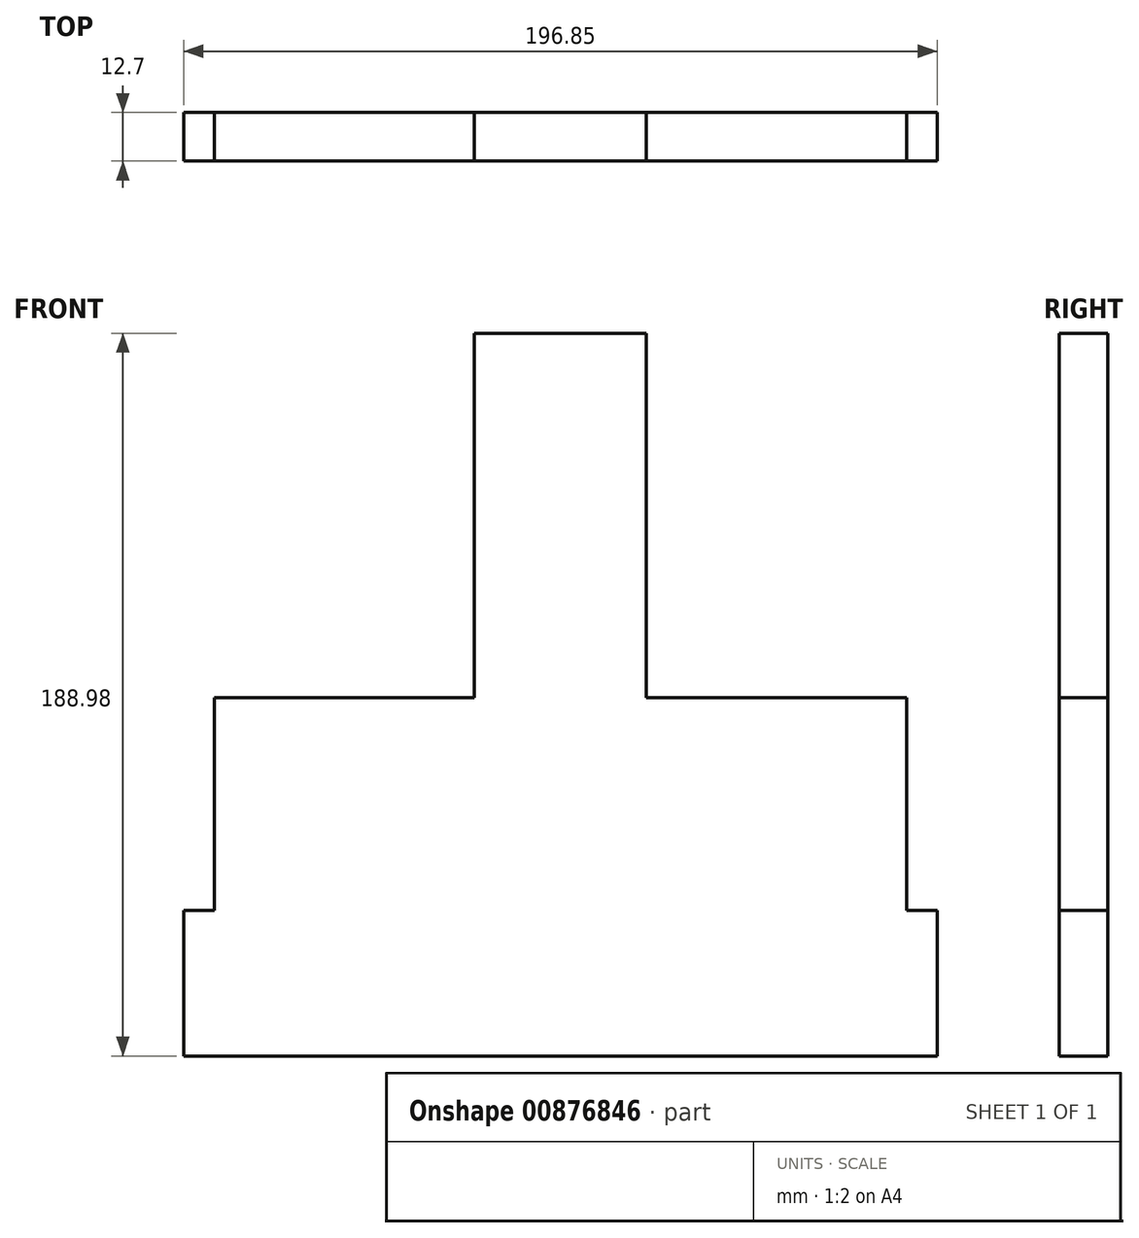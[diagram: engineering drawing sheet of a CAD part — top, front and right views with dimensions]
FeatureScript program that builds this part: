
annotation { "Feature Type Name" : "Feature", "Feature Type Description" : "" }
export const myFeature = defineFeature(function(context is Context, id is Id, definition is map)
    precondition{}
    {
        {
            var Q0;
            Q0=qCreatedBy(makeId("Front.planeOp"),FACE);
            var sketch = newSketch(context, id + "F0", { "sketchPlane" : qUnion([Q0])});
            skLineSegment(sketch, "E0.bottom", {"start": v(0, 0) * mm, "end": v(196.85, 0) * mm});
            skLineSegment(sketch, "E0.top", {"start": v(0, 38.1) * mm, "end": v(196.85, 38.1) * mm});
            skLineSegment(sketch, "E0.left", {"start": v(0, 0) * mm, "end": v(0, 38.1) * mm});
            skLineSegment(sketch, "E0.right", {"start": v(196.85, 0) * mm, "end": v(196.85, 38.1) * mm});
            skLineSegment(sketch, "E1.bottom", {"start": v(7.94, 38.1) * mm, "end": v(188.91, 38.1) * mm});
            skLineSegment(sketch, "E1.top", {"start": v(7.94, 93.73) * mm, "end": v(188.91, 93.73) * mm});
            skLineSegment(sketch, "E1.left", {"start": v(7.94, 38.1) * mm, "end": v(7.94, 93.73) * mm});
            skLineSegment(sketch, "E1.right", {"start": v(188.91, 38.1) * mm, "end": v(188.91, 93.73) * mm});
            skLineSegment(sketch, "E2.bottom", {"start": v(75.88, 93.73) * mm, "end": v(120.84, 93.73) * mm});
            skLineSegment(sketch, "E2.top", {"start": v(75.88, 188.98) * mm, "end": v(120.84, 188.98) * mm});
            skLineSegment(sketch, "E2.left", {"start": v(75.88, 93.73) * mm, "end": v(75.88, 188.98) * mm});
            skLineSegment(sketch, "E2.right", {"start": v(120.84, 93.73) * mm, "end": v(120.84, 188.98) * mm});
            skSolve(sketch);
        }
        {
            var Q0;
            Q0 = qSketchRegion(id + "F0", true);
            extrude(context, id + "F1", {"entities" : qUnion([Q0]), "depth" : 12.7 * mm, "offsetDistance" : 25.4 * mm});
        }
    });
